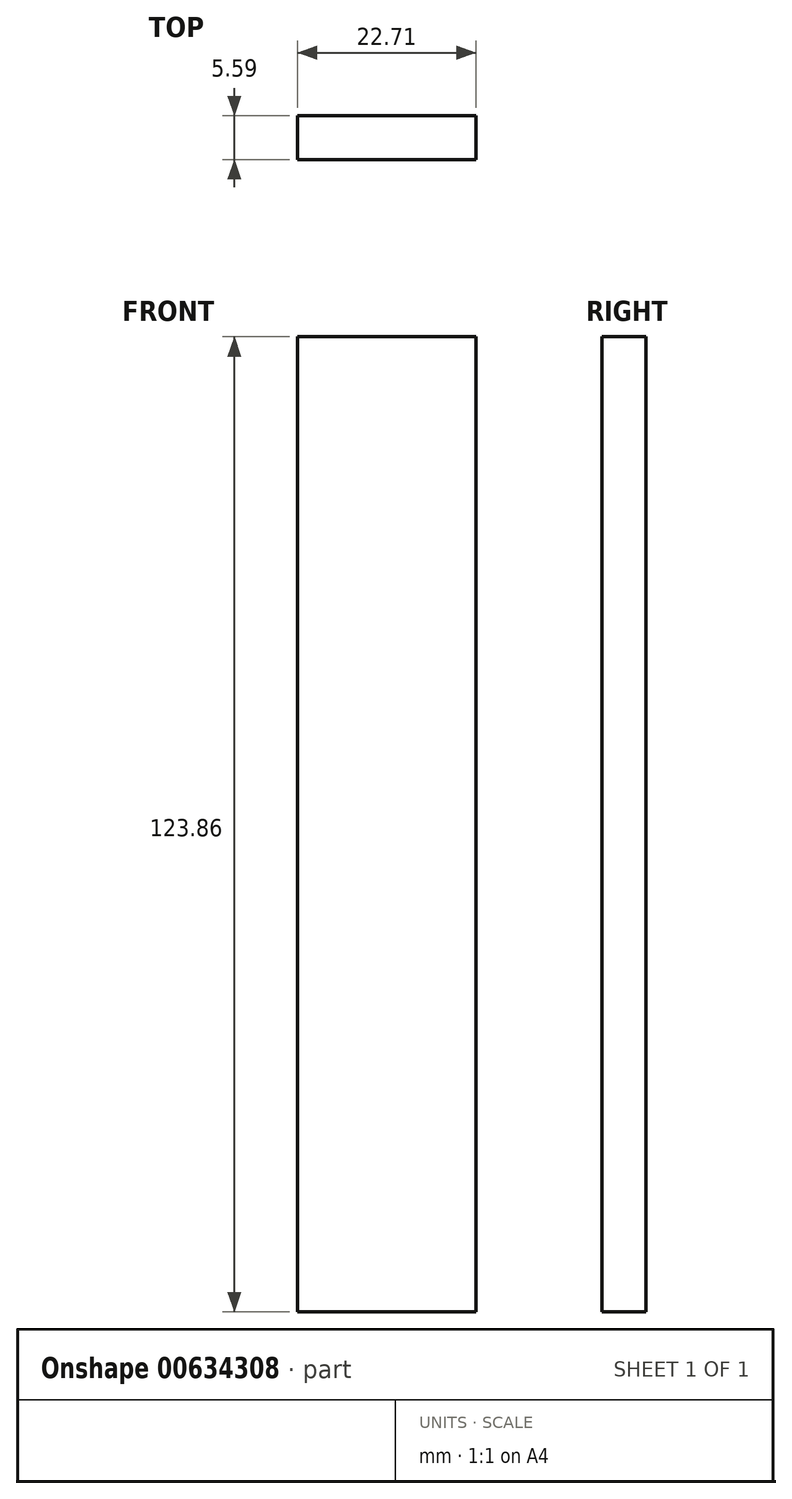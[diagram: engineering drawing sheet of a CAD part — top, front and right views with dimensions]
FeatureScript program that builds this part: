
annotation { "Feature Type Name" : "Feature", "Feature Type Description" : "" }
export const myFeature = defineFeature(function(context is Context, id is Id, definition is map)
    precondition{}
    {
        {
            var Q0;
            Q0=qCreatedBy(makeId("Front.planeOp"),FACE);
            var sketch = newSketch(context, id + "F0", { "sketchPlane" : qUnion([Q0])});
            skLineSegment(sketch, "E0.bottom", {"start": v(-13.94, 55.22) * mm, "end": v(8.77, 55.22) * mm});
            skLineSegment(sketch, "E0.top", {"start": v(-13.94, -68.64) * mm, "end": v(8.77, -68.64) * mm});
            skLineSegment(sketch, "E0.left", {"start": v(-13.94, 55.22) * mm, "end": v(-13.94, -68.64) * mm});
            skLineSegment(sketch, "E0.right", {"start": v(8.77, 55.22) * mm, "end": v(8.77, -68.64) * mm});
            skSolve(sketch);
        }
        {
            var Q0;
            Q0 = qSketchRegion(id + "F0", true);
            extrude(context, id + "F1", {"entities" : qUnion([Q0]), "depth" : 5.6 * mm, "offsetDistance" : 25.4 * mm});
        }
    });
